# Revit family: ALRM-Intellect
name_source: partatom
category: Lighting Fixtures
units: mm (PartAtom-declared; Revit-internal decimal feet)

## family parameters
Always vertical = Yes
Cut with Voids When Loaded = No
Host = Ceiling
Light Source = Yes
OmniClass Number = 23.80.70.11.14.17
OmniClass Title = Direct/Indirect
Part Type = Normal
Room Calculation Point = No
Round Connector Dimension = Use Diameter
Shared = No

## types (6) — shared parameters
Assembly Code = D5020200
Color Filter = 16777215
Description = Intellect Enabled LED ALLURA Linear Pendant Type M
Dimming Lamp Color Temperature Shift = <None>
Housing Finish = Metal - Viscor - White
Lamp = LED
Lens Finish Bottom = Acrylic - Viscor - Frosted
Lens Finish Top = Acrylic - Viscor - Clear
Manufacturer = VISIONEERING by VISCOR
Model = ALRM-Intellect
Tilt Angle = 180.00°
URL = https://www.viscor.com
Voltage = 120 V
Width = 0' - 9"

## per-type parameters (varying)
| type | Apparent Load | Emit from Line Length | Lamp Wattage | Length | Photometric Web File |
| ALRM48-LED840K032LUNV-C91V99(LV01) | 24 VA | 4' - 0" | 24 VA | 4' - 0" | ALRM48-LED840K032LUNV-C91V99(LV01).IES |
| ALRM96-LED840K064LUNV-C91V99(LV01) | 43 VA | 8' - 0" | 43 VA | 8' - 0" | ALRM96-LED840K064LUNV-C91V99(LV01).ies |
| ALRM48-LED840K052LUNV-C91V99(LV01) | 39 VA | 4' - 0" | 39 VA | 4' - 0" | ALRM48-LED840K052LUNV-C91V99(LV01).IES |
| ALRM48-LED840K060LUNV-C91V99(LV01) | 45 VA | 4' - 0" | 45 VA | 4' - 0" | ALRM48-LED840K060LUNV-C91V99(LV01).IES |
| ALRM96-LED840K105LUNV-C91V99(LV01) | 77 VA | 8' - 0" | 77 VA | 8' - 0" | ALRM96-LED840K105LUNV-C91V99(LV01).ies |
| ALRM96-LED840K120LUNV-C91V99(LV01) | 90 VA | 8' - 0" | 90 VA | 8' - 0" | ALRM96-LED840K120LUNV-C91V99(LV01).ies |

## geometry (parser evidence)
native form markers: Sweep x2
no freeform markers — native parametric forms only
